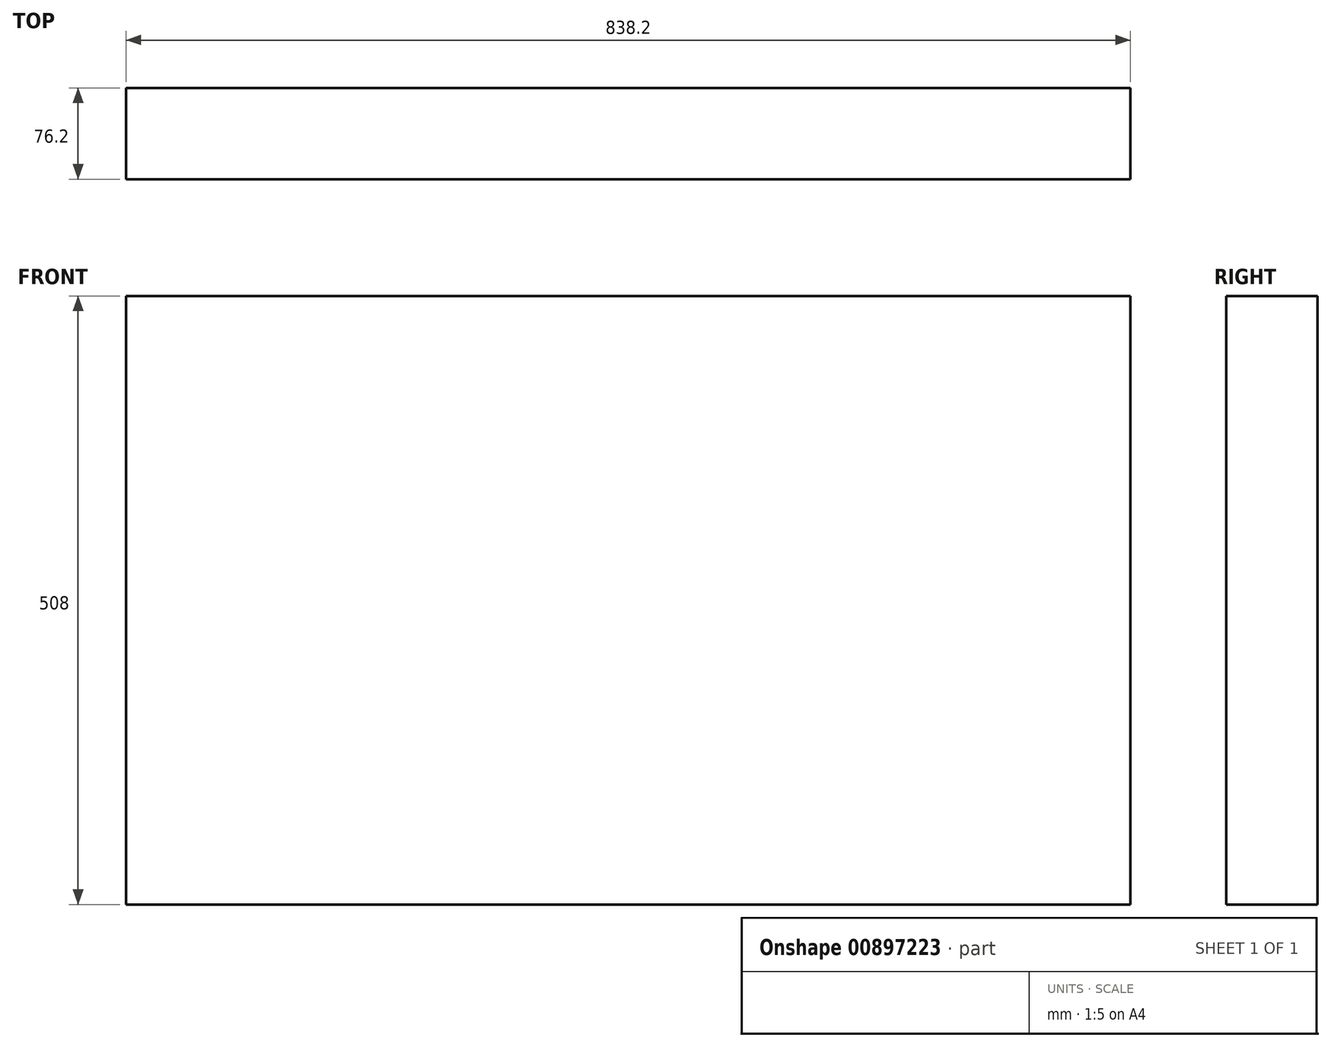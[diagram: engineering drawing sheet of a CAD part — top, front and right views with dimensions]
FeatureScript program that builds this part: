
annotation { "Feature Type Name" : "Feature", "Feature Type Description" : "" }
export const myFeature = defineFeature(function(context is Context, id is Id, definition is map)
    precondition{}
    {
        {
            var Q0;
            Q0=qCreatedBy(makeId("Front.planeOp"),FACE);
            var sketch = newSketch(context, id + "F0", { "sketchPlane" : qUnion([Q0])});
            skLineSegment(sketch, "E0.bottom", {"start": v(0, 0) * mm, "end": v(838.2, 0) * mm});
            skLineSegment(sketch, "E0.top", {"start": v(0, 508) * mm, "end": v(838.2, 508) * mm});
            skLineSegment(sketch, "E0.left", {"start": v(0, 0) * mm, "end": v(0, 508) * mm});
            skLineSegment(sketch, "E0.right", {"start": v(838.2, 0) * mm, "end": v(838.2, 508) * mm});
            skSolve(sketch);
        }
        {
            var Q0;
            Q0 = qSketchRegion(id + "F0", true);
            extrude(context, id + "F1", {"entities" : qUnion([Q0]), "oppositeDirection" : true, "depth" : 76.2 * mm, "offsetDistance" : 25.4 * mm});
        }
    });
